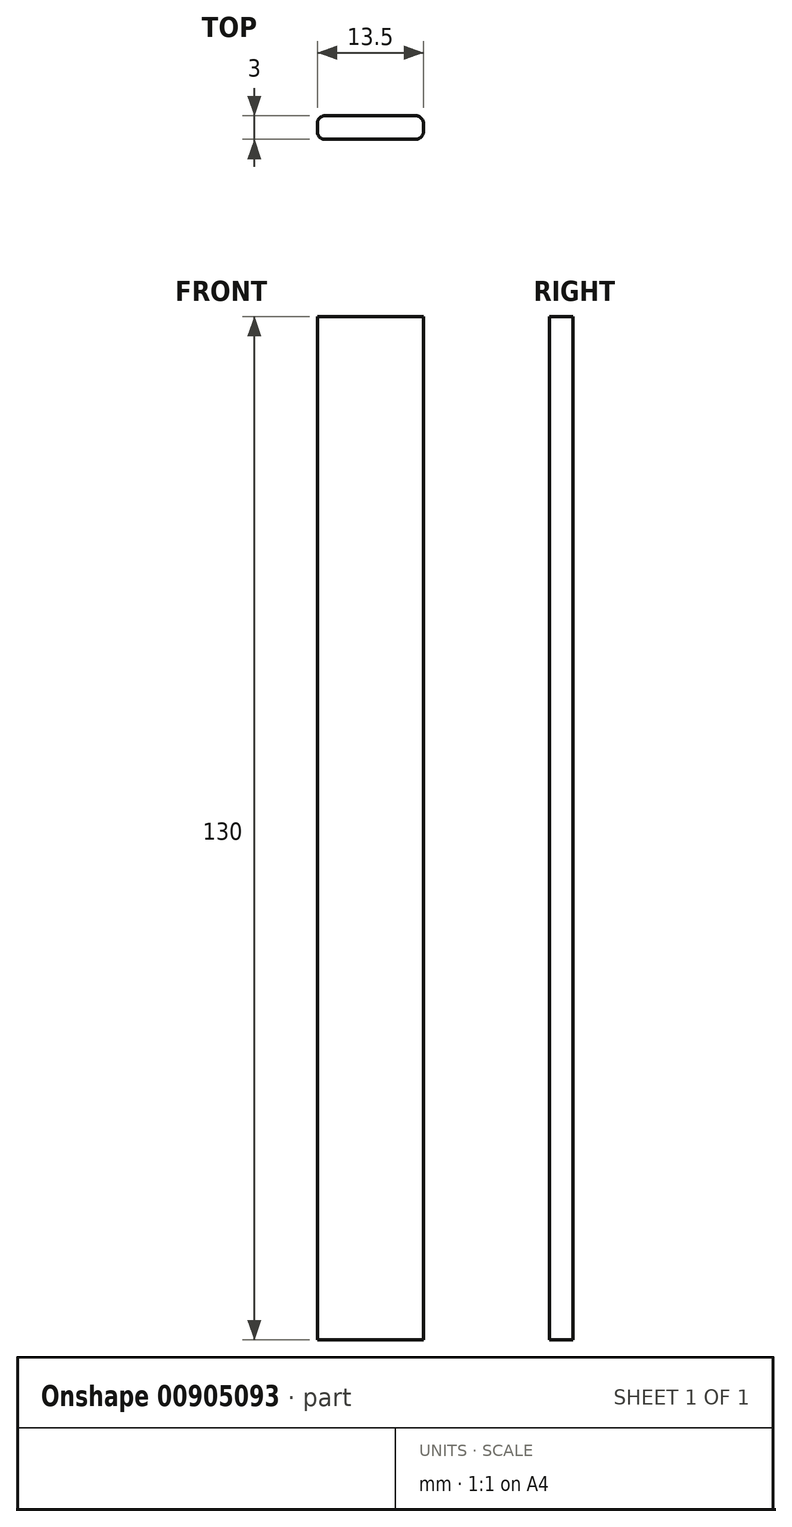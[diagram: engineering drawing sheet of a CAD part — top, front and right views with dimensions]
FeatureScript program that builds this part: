
annotation { "Feature Type Name" : "Feature", "Feature Type Description" : "" }
export const myFeature = defineFeature(function(context is Context, id is Id, definition is map)
    precondition{}
    {
        {
            var Q0;
            Q0=qCreatedBy(makeId("Top.planeOp"),FACE);
            var sketch = newSketch(context, id + "F0", { "sketchPlane" : qUnion([Q0])});
            skLineSegment(sketch, "E0.bottom", {"start": v(-5.75, 1.5) * mm, "end": v(5.75, 1.5) * mm});
            skLineSegment(sketch, "E0.top", {"start": v(-5.75, -1.5) * mm, "end": v(5.75, -1.5) * mm});
            skLineSegment(sketch, "E0.left", {"start": v(-6.75, 0.5) * mm, "end": v(-6.75, -0.5) * mm});
            skLineSegment(sketch, "E0.right", {"start": v(6.75, 0.5) * mm, "end": v(6.75, -0.5) * mm});
            skPoint(sketch, "E0.middle", {"position": v(0, 0) * mm});
            skPoint(sketch, "E1.visualSharp", {"position": v(-6.75, 1.5) * mm});
            skArc(sketch, "E1.filletArc", {"start": v(-5.75, 1.5) * mm, "mid": v(-6.46, 1.2) * mm, "end": v(-6.75, 0.5) * mm});
            skPoint(sketch, "E2.visualSharp", {"position": v(-6.75, -1.5) * mm});
            skArc(sketch, "E2.filletArc", {"start": v(-6.75, -0.5) * mm, "mid": v(-6.46, -1.2) * mm, "end": v(-5.75, -1.5) * mm});
            skPoint(sketch, "E3.visualSharp", {"position": v(6.75, -1.5) * mm});
            skArc(sketch, "E3.filletArc", {"start": v(5.75, -1.5) * mm, "mid": v(6.46, -1.2) * mm, "end": v(6.75, -0.5) * mm});
            skPoint(sketch, "E4.visualSharp", {"position": v(6.75, 1.5) * mm});
            skArc(sketch, "E4.filletArc", {"start": v(6.75, 0.5) * mm, "mid": v(6.46, 1.2) * mm, "end": v(5.75, 1.5) * mm});
            skSolve(sketch);
        }
        {
            var Q0;
            Q0 = qSketchRegion(id + "F0", true);
            extrude(context, id + "F1", {"entities" : qUnion([Q0]), "depth" : 130 * mm, "offsetDistance" : 25 * mm});
        }
    });
